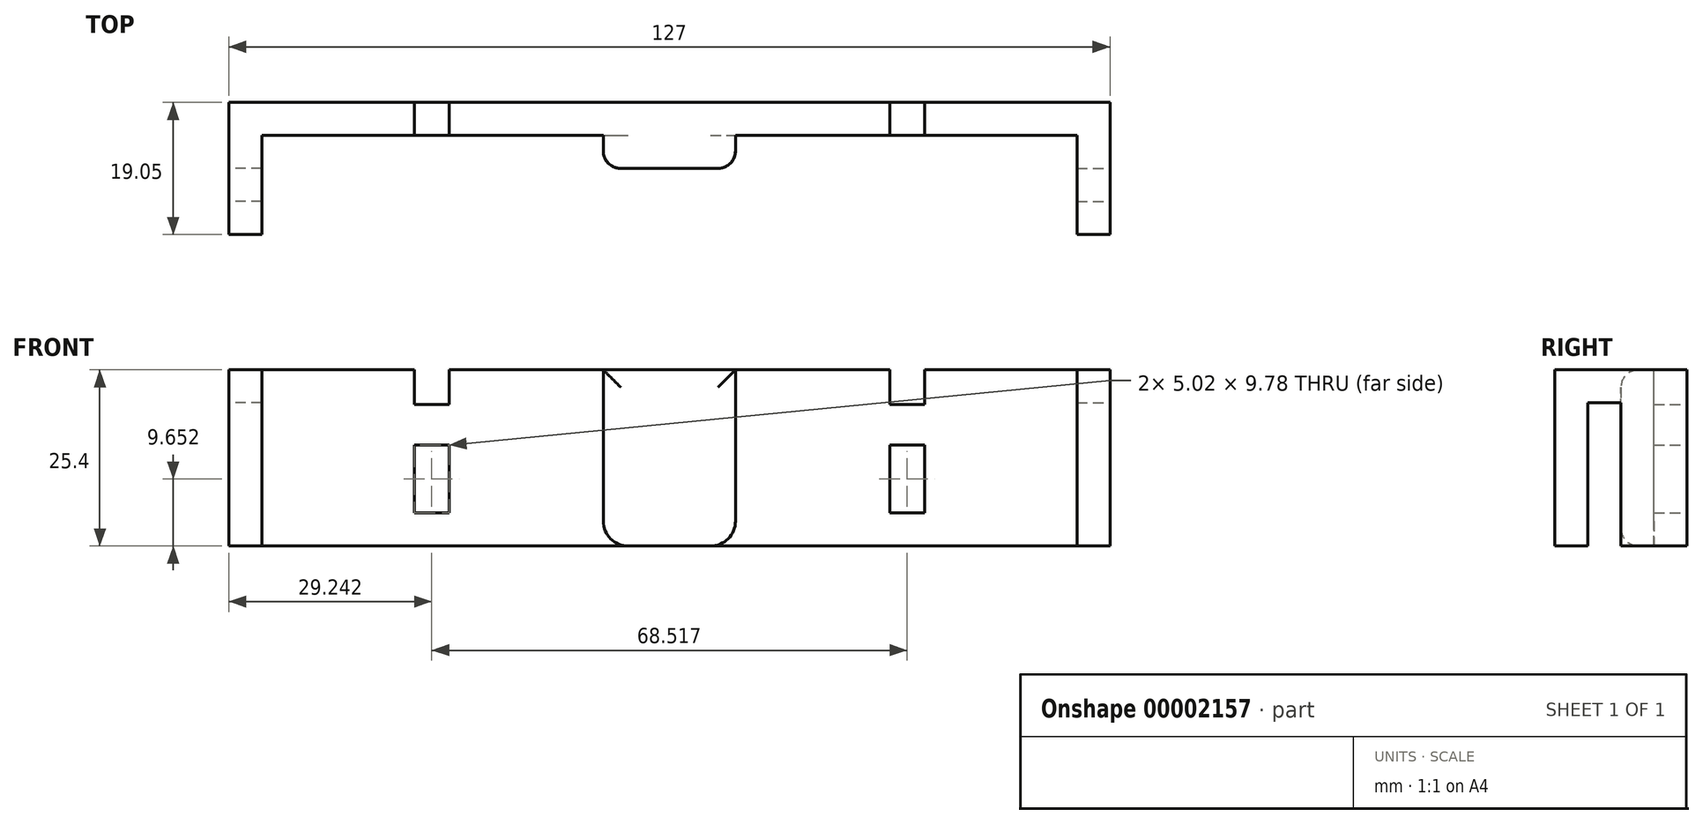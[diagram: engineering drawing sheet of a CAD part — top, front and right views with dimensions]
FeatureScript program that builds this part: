
annotation { "Feature Type Name" : "Feature", "Feature Type Description" : "" }
export const myFeature = defineFeature(function(context is Context, id is Id, definition is map)
    precondition{}
    {
        {
            var Q0;
            Q0=qCreatedBy(makeId("Front.planeOp"),FACE);
            var sketch = newSketch(context, id + "F0", { "sketchPlane" : qUnion([Q0])});
            skLineSegment(sketch, "E0.bottom", {"start": v(0, 0) * mm, "end": v(127, 0) * mm});
            skLineSegment(sketch, "E0.top", {"start": v(0, 25.4) * mm, "end": v(127, 25.4) * mm});
            skLineSegment(sketch, "E0.left", {"start": v(0, 0) * mm, "end": v(0, 25.4) * mm});
            skLineSegment(sketch, "E0.right", {"start": v(127, 0) * mm, "end": v(127, 25.4) * mm});
            skSolve(sketch);
        }
        {
            var Q0;
            Q0=makeQuery(id+"F0.imprint","IMPRINT",FACE,{"disambiguationData":[TD([[makeQuery(id+"F0.imprint","IMPRINT",EDGE,{"derivedFrom":sQuery(id+"F0.wireOp",EDGE,"E0.bottom")}),1.0]])]});
            extrude(context, id + "F1", {"entities" : qUnion([Q0]), "depth" : 4.76 * mm});
        }
        {
            var Q0;
            Q0=makeQuery(id+"F1.opExtrude","SWEPT_FACE",FACE,{"disambiguationData":[OSD([sQuery(id+"F0.wireOp",EDGE,"E0.right")])]});
            var sketch = newSketch(context, id + "F2", { "sketchPlane" : qUnion([Q0])});
            skLineSegment(sketch, "E1", {"start": v(-4.76, 25.4) * mm, "end": v(-19.05, 25.4) * mm});
            skLineSegment(sketch, "E2", {"start": v(-19.05, 25.4) * mm, "end": v(-19.05, 0) * mm});
            skLineSegment(sketch, "E3", {"start": v(-19.05, 0) * mm, "end": v(-14.29, 0) * mm});
            skLineSegment(sketch, "E4", {"start": v(-14.29, 0) * mm, "end": v(-14.29, 20.64) * mm});
            skLineSegment(sketch, "E5", {"start": v(-14.29, 20.64) * mm, "end": v(-9.53, 20.64) * mm});
            skLineSegment(sketch, "E6", {"start": v(-9.53, 20.64) * mm, "end": v(-9.53, 0) * mm});
            skLineSegment(sketch, "E7", {"start": v(-9.53, 0) * mm, "end": v(-4.76, 0) * mm});
            skLineSegment(sketch, "E8", {"start": v(-4.76, 0) * mm, "end": v(-4.76, 25.4) * mm});
            skSolve(sketch);
        }
        {
            var Q0;
            Q0=makeQuery(id+"F2.imprint","IMPRINT",FACE,{"disambiguationData":[TD([[makeQuery(id+"F2.imprint","IMPRINT",EDGE,{"derivedFrom":sQuery(id+"F2.wireOp",EDGE,"E1")}),1.0]])]});
            extrude(context, id + "F3", {"entities" : qUnion([Q0]), "operationType" : NewBodyOperationType.ADD, "oppositeDirection" : true, "depth" : 4.76 * mm});
        }
        {
            var Q0;
            Q0=makeQuery(id+"F1.opExtrude","SWEPT_FACE",FACE,{"disambiguationData":[OSD([sQuery(id+"F0.wireOp",EDGE,"E0.left")])]});
            var sketch = newSketch(context, id + "F4", { "sketchPlane" : qUnion([Q0])});
            skLineSegment(sketch, "E9.0.0", {"start": v(4.76, 0) * mm, "end": v(4.76, 25.4) * mm});
            skLineSegment(sketch, "E9.0.1", {"start": v(9.53, 0) * mm, "end": v(4.76, 0) * mm});
            skLineSegment(sketch, "E9.0.2", {"start": v(9.53, 20.64) * mm, "end": v(9.53, 0) * mm});
            skLineSegment(sketch, "E9.0.3", {"start": v(14.29, 20.64) * mm, "end": v(9.53, 20.64) * mm});
            skLineSegment(sketch, "E9.0.4", {"start": v(14.29, 0) * mm, "end": v(14.29, 20.64) * mm});
            skLineSegment(sketch, "E9.0.5", {"start": v(19.05, 0) * mm, "end": v(14.29, 0) * mm});
            skLineSegment(sketch, "E9.0.6", {"start": v(19.05, 25.4) * mm, "end": v(19.05, 0) * mm});
            skLineSegment(sketch, "E9.0.7", {"start": v(4.76, 25.4) * mm, "end": v(19.05, 25.4) * mm});
            skSolve(sketch);
        }
        {
            var Q0;
            Q0=makeQuery(id+"F4.imprint","IMPRINT",FACE,{"disambiguationData":[TD([[makeQuery(id+"F4.imprint","IMPRINT",EDGE,{"derivedFrom":sQuery(id+"F4.wireOp",EDGE,"E9.0.0")}),-1.0]])]});
            extrude(context, id + "F5", {"entities" : qUnion([Q0]), "operationType" : NewBodyOperationType.ADD, "oppositeDirection" : true, "depth" : 4.76 * mm});
        }
        {
            var Q0;
            Q0=makeQuery(id+"F1.opExtrude","CAP_FACE",FACE,{"disambiguationData":[OSD([sQuery(id+"F0.wireOp",EDGE,"E0.bottom"),sQuery(id+"F0.wireOp",EDGE,"E0.top"),sQuery(id+"F0.wireOp",EDGE,"E0.left"),sQuery(id+"F0.wireOp",EDGE,"E0.right")])],"isStart":false});
            var sketch = newSketch(context, id + "F6", { "sketchPlane" : qUnion([Q0])});
            skLineSegment(sketch, "E10", {"start": v(63.5, 25.4) * mm, "end": v(63.5, 0) * mm, "construction": true});
            skPoint(sketch, "E11", {"position": v(63.5, 12.7) * mm});
            skLineSegment(sketch, "E12.bottom", {"start": v(57.58, 25.4) * mm, "end": v(73.02, 25.4) * mm});
            skLineSegment(sketch, "E12.top", {"start": v(57.58, 0) * mm, "end": v(69.42, 0) * mm});
            skLineSegment(sketch, "E12.left", {"start": v(53.97, 21.8) * mm, "end": v(53.97, 3.6) * mm});
            skLineSegment(sketch, "E12.right", {"start": v(73.02, 25.4) * mm, "end": v(73.02, 3.6) * mm});
            skLineSegment(sketch, "E13", {"start": v(53.97, 25.4) * mm, "end": v(73.03, 0) * mm, "construction": true});
            skPoint(sketch, "E14.visualSharp", {"position": v(53.97, 25.4) * mm});
            skPoint(sketch, "E15.visualSharp", {"position": v(73.02, 25.4) * mm});
            skPoint(sketch, "E16.visualSharp", {"position": v(73.02, 0) * mm});
            skArc(sketch, "E16.filletArc", {"start": v(69.42, 0) * mm, "mid": v(71.97, 1.05) * mm, "end": v(73.02, 3.6) * mm});
            skPoint(sketch, "E17.visualSharp", {"position": v(53.97, 0) * mm});
            skArc(sketch, "E17.filletArc", {"start": v(53.97, 3.6) * mm, "mid": v(55.03, 1.05) * mm, "end": v(57.58, 0) * mm});
            skLineSegment(sketch, "E18", {"start": v(57.58, 25.4) * mm, "end": v(53.97, 25.4) * mm});
            skLineSegment(sketch, "E19", {"start": v(53.97, 21.8) * mm, "end": v(53.97, 25.4) * mm});
            skSolve(sketch);
        }
        {
            var Q0;
            Q0=makeQuery(id+"F6.imprint","IMPRINT",FACE,{"disambiguationData":[TD([[makeQuery(id+"F6.imprint","IMPRINT",EDGE,{"derivedFrom":sQuery(id+"F6.wireOp",EDGE,"E12.bottom")}),-1.0]])]});
            extrude(context, id + "F7", {"entities" : qUnion([Q0]), "operationType" : NewBodyOperationType.ADD, "depth" : 4.76 * mm});
        }
        {
            var Q0;
            Q0=makeQuery(id+"F7.opExtrude","CAP_FACE",FACE,{"disambiguationData":[OSD([sQuery(id+"F6.wireOp",EDGE,"E12.bottom"),sQuery(id+"F6.wireOp",EDGE,"E12.top"),sQuery(id+"F6.wireOp",EDGE,"E12.left"),sQuery(id+"F6.wireOp",EDGE,"E12.right"),sQuery(id+"F6.wireOp",EDGE,"E16.filletArc"),sQuery(id+"F6.wireOp",EDGE,"E17.filletArc"),sQuery(id+"F6.wireOp",EDGE,"E19")])],"isStart":false});
            fillet(context, id + "F8", {"entities" : qUnion([Q0]), "radius" : 2.54 * mm, "tangentPropagation" : true, "allowEdgeOverflow" : false});
        }
        {
            var Q0;
            Q0=makeQuery(id+"F1.opExtrude","CAP_FACE",FACE,{"disambiguationData":[OSD([sQuery(id+"F0.wireOp",EDGE,"E0.bottom"),sQuery(id+"F0.wireOp",EDGE,"E0.top"),sQuery(id+"F0.wireOp",EDGE,"E0.left"),sQuery(id+"F0.wireOp",EDGE,"E0.right")])],"isStart":true});
            var sketch = newSketch(context, id + "F9", { "sketchPlane" : qUnion([Q0])});
            skLineSegment(sketch, "E20", {"start": v(-63.5, 25.4) * mm, "end": v(-63.5, 0) * mm, "construction": true});
            skLineSegment(sketch, "E21", {"start": v(-95.25, 25.4) * mm, "end": v(-95.25, 0) * mm, "construction": true});
            skLineSegment(sketch, "E22", {"start": v(-31.75, 25.4) * mm, "end": v(-31.75, 0) * mm, "construction": true});
            skLineSegment(sketch, "E23.bottom", {"start": v(-95.25, 25.4) * mm, "end": v(-100.27, 25.4) * mm});
            skLineSegment(sketch, "E23.top", {"start": v(-95.25, 20.38) * mm, "end": v(-100.27, 20.38) * mm});
            skLineSegment(sketch, "E23.left", {"start": v(-95.25, 25.4) * mm, "end": v(-95.25, 20.38) * mm});
            skLineSegment(sketch, "E23.right", {"start": v(-100.27, 25.4) * mm, "end": v(-100.27, 20.38) * mm});
            skLineSegment(sketch, "E24.bottom", {"start": v(-95.25, 14.54) * mm, "end": v(-100.27, 14.54) * mm});
            skLineSegment(sketch, "E24.top", {"start": v(-95.25, 4.76) * mm, "end": v(-100.27, 4.76) * mm});
            skLineSegment(sketch, "E24.left", {"start": v(-95.25, 14.54) * mm, "end": v(-95.25, 4.76) * mm});
            skLineSegment(sketch, "E24.right", {"start": v(-100.27, 14.54) * mm, "end": v(-100.27, 4.76) * mm});
            skLineSegment(sketch, "E25.0.MirrorCS", {"start": v(-31.75, 25.4) * mm, "end": v(-26.73, 25.4) * mm});
            skLineSegment(sketch, "E25.1.MirrorCS", {"start": v(-31.75, 20.38) * mm, "end": v(-26.73, 20.38) * mm});
            skLineSegment(sketch, "E25.2.MirrorCS", {"start": v(-31.75, 14.54) * mm, "end": v(-31.75, 4.76) * mm});
            skLineSegment(sketch, "E25.3.MirrorCS", {"start": v(-26.73, 14.54) * mm, "end": v(-26.73, 4.76) * mm});
            skLineSegment(sketch, "E25.4.MirrorCS", {"start": v(-31.75, 14.54) * mm, "end": v(-26.73, 14.54) * mm});
            skLineSegment(sketch, "E25.5.MirrorCS", {"start": v(-31.75, 4.76) * mm, "end": v(-26.73, 4.76) * mm});
            skLineSegment(sketch, "E25.6.MirrorCS", {"start": v(-26.73, 25.4) * mm, "end": v(-26.73, 20.38) * mm});
            skLineSegment(sketch, "E25.7.MirrorCS", {"start": v(-31.75, 25.4) * mm, "end": v(-31.75, 20.38) * mm});
            skSolve(sketch);
        }
        {
            var Q0;
            {Q0=qUnion([makeQuery(id+"F9.imprint","IMPRINT",FACE,{"disambiguationData":[TD([[makeQuery(id+"F9.imprint","IMPRINT",EDGE,{"derivedFrom":sQuery(id+"F9.wireOp",EDGE,"E23.bottom")}),1.0]])]}),makeQuery(id+"F9.imprint","IMPRINT",FACE,{"disambiguationData":[TD([[makeQuery(id+"F9.imprint","IMPRINT",EDGE,{"derivedFrom":sQuery(id+"F9.wireOp",EDGE,"E24.bottom")}),1.0]])]}),makeQuery(id+"F9.imprint","IMPRINT",FACE,{"disambiguationData":[TD([[makeQuery(id+"F9.imprint","IMPRINT",EDGE,{"derivedFrom":sQuery(id+"F9.wireOp",EDGE,"E25.0.MirrorCS")}),1.0]])]}),makeQuery(id+"F9.imprint","IMPRINT",FACE,{"disambiguationData":[TD([[makeQuery(id+"F9.imprint","IMPRINT",EDGE,{"derivedFrom":sQuery(id+"F9.wireOp",EDGE,"E25.2.MirrorCS")}),1.0]])]})]);}
            extrude(context, id + "F10", {"entities" : qUnion([Q0]), "operationType" : NewBodyOperationType.REMOVE, "oppositeDirection" : true, "depth" : 25.4 * mm});
        }
    });
